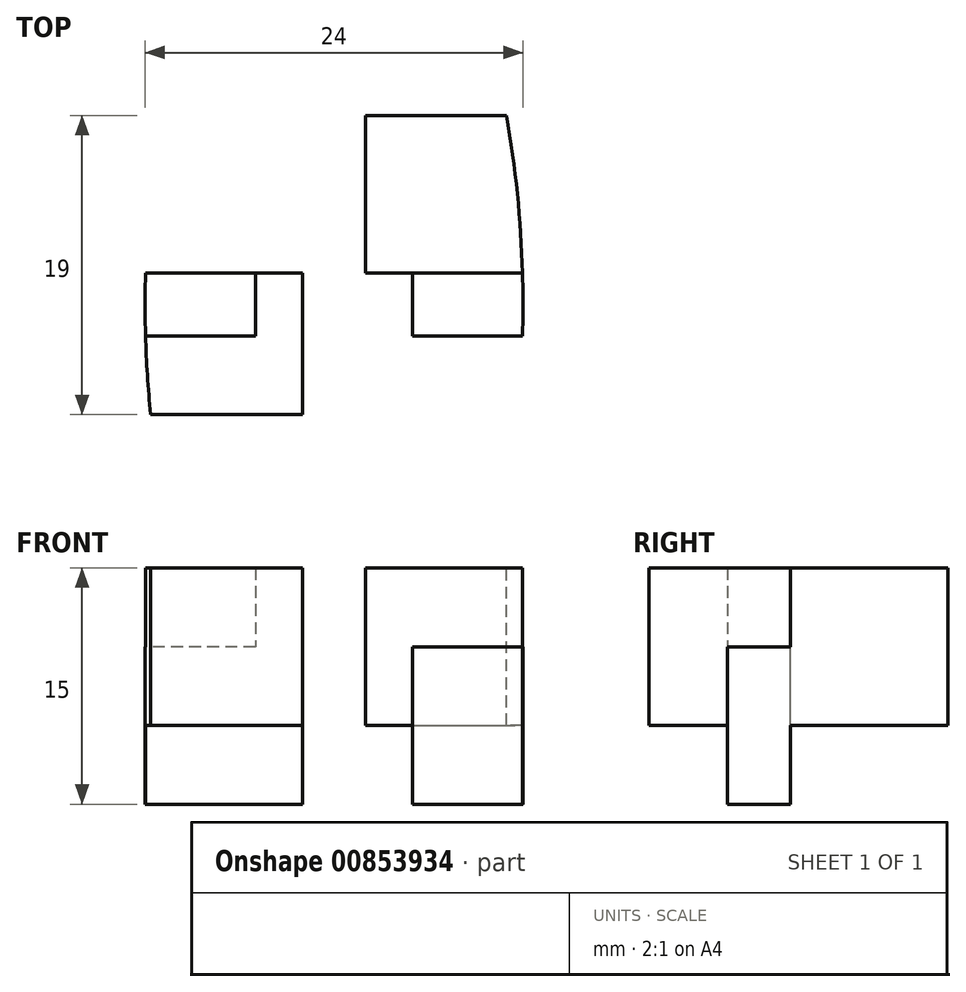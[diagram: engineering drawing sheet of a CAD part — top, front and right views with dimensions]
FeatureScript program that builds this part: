
annotation { "Feature Type Name" : "Feature", "Feature Type Description" : "" }
export const myFeature = defineFeature(function(context is Context, id is Id, definition is map)
    precondition{}
    {
        {
            var Q0;
            Q0=qCreatedBy(makeId("Top.planeOp"),FACE);
            var sketch = newSketch(context, id + "F0", { "sketchPlane" : qUnion([Q0])});
            skCircle(sketch, "E0", {"center": v(0, 57) * mm, "radius": 2 * mm});
            skLineSegment(sketch, "E1", {"start": v(12, 0) * mm, "end": v(57, 0) * mm});
            skLineSegment(sketch, "E2", {"start": v(0, 12) * mm, "end": v(-10.95, 12) * mm});
            skLineSegment(sketch, "E3", {"start": v(-10.95, 12) * mm, "end": v(10.95, 12) * mm});
            skLineSegment(sketch, "E4", {"start": v(0, -7) * mm, "end": v(-11.64, -7) * mm});
            skLineSegment(sketch, "E5", {"start": v(-11.64, -7) * mm, "end": v(-2, -7) * mm});
            skLineSegment(sketch, "E6", {"start": v(0, -2) * mm, "end": v(11.97, -2) * mm});
            skLineSegment(sketch, "E7", {"start": v(11.97, -2) * mm, "end": v(-11.97, -2) * mm});
            skLineSegment(sketch, "E8", {"start": v(0, 2) * mm, "end": v(-11.97, 2) * mm});
            skLineSegment(sketch, "E9", {"start": v(-11.97, 2) * mm, "end": v(11.97, 2) * mm});
            skLineSegment(sketch, "E10", {"start": v(0, 2) * mm, "end": v(-2, 2) * mm});
            skLineSegment(sketch, "E11", {"start": v(-2, 2) * mm, "end": v(-2, 57) * mm});
            skLineSegment(sketch, "E12", {"start": v(-2, 57) * mm, "end": v(2, 57) * mm});
            skLineSegment(sketch, "E13", {"start": v(2, 57) * mm, "end": v(2, 2) * mm});
            skCircle(sketch, "E14", {"center": v(0, -57) * mm, "radius": 2 * mm});
            skLineSegment(sketch, "E15", {"start": v(2, 2) * mm, "end": v(2, -57) * mm});
            skLineSegment(sketch, "E16", {"start": v(-2, 2) * mm, "end": v(-2, -57) * mm});
            skLineSegment(sketch, "E17", {"start": v(-5, 0) * mm, "end": v(-5, 57) * mm});
            skLineSegment(sketch, "E18", {"start": v(5, 0) * mm, "end": v(5, -57) * mm});
            skLineSegment(sketch, "E19", {"start": v(-5, 0) * mm, "end": v(-5, -57) * mm});
            skArc(sketch, "E20", {"start": v(5, -57) * mm, "mid": v(0, -62) * mm, "end": v(-5, -57) * mm});
            skLineSegment(sketch, "E21", {"start": v(5, 0) * mm, "end": v(5, 57) * mm});
            skArc(sketch, "E22", {"start": v(-5, 57) * mm, "mid": v(0, 62) * mm, "end": v(5, 57) * mm});
            skLineSegment(sketch, "E23.trimOffspring", {"start": v(0, -7) * mm, "end": v(11.64, -7) * mm});
            skLineSegment(sketch, "E24.trimOffspring", {"start": v(0, -55) * mm, "end": v(0, -57) * mm});
            skArc(sketch, "E25.trimOffspring", {"start": v(11.64, -7) * mm, "mid": v(11.95, 2.52) * mm, "end": v(10.95, 12) * mm});
            skArc(sketch, "E26.trimOffspring", {"start": v(-10.95, 12) * mm, "mid": v(-11.95, 2.52) * mm, "end": v(-11.64, -7) * mm});
            skLineSegment(sketch, "E27.trimOffspring", {"start": v(0, 55) * mm, "end": v(0, 57) * mm});
            skLineSegment(sketch, "E28.trimOffspring", {"start": v(-12, 0) * mm, "end": v(-57, 0) * mm});
            skSolve(sketch);
        }
        {
            var Q0;
            {var subQ0=sQuery(id+"F0.wireOp",EDGE,"E26.trimOffspring");var subQ1=sQuery(id+"F0.wireOp",EDGE,"E3");var subQ2=makeQuery(id+"F0.imprint","INTERSECT",VERTEX,{"derivedFrom":[subQ1,subQ0]});Q0=makeQuery(id+"F0.imprint","IMPRINT",FACE,{"disambiguationData":[TD([[makeQuery(id+"F0.imprint","IMPRINT",EDGE,{"disambiguationData":[TD([[subQ2,-1.0]])],"derivedFrom":subQ1}),-1.0]])]});}
            var Q1;
            {var subQ0=sQuery(id+"F0.wireOp",EDGE,"E26.trimOffspring");var subQ1=sQuery(id+"F0.wireOp",EDGE,"E5");var subQ2=makeQuery(id+"F0.imprint","INTERSECT",VERTEX,{"derivedFrom":[subQ1,subQ0]});Q1=makeQuery(id+"F0.imprint","IMPRINT",FACE,{"disambiguationData":[TD([[makeQuery(id+"F0.imprint","IMPRINT",EDGE,{"disambiguationData":[TD([[subQ2,-1.0]])],"derivedFrom":subQ1}),1.0]])]});}
            var Q2;
            {var subQ0=sQuery(id+"F0.wireOp",EDGE,"E16");var subQ5=sQuery(id+"F0.wireOp",EDGE,"E7");var subQ6=makeQuery(id+"F0.imprint","INTERSECT",VERTEX,{"derivedFrom":[subQ5,subQ0]});Q2=makeQuery(id+"F0.imprint","IMPRINT",FACE,{"disambiguationData":[TD([[makeQuery(id+"F0.imprint","IMPRINT",EDGE,{"disambiguationData":[TD([[subQ6,-1.0]])],"derivedFrom":subQ5}),1.0]])]});}
            var Q3;
            {var subQ0=sQuery(id+"F0.wireOp",EDGE,"E18");var subQ1=sQuery(id+"F0.wireOp",EDGE,"E7");var subQ2=makeQuery(id+"F0.imprint","INTERSECT",VERTEX,{"derivedFrom":[subQ1,subQ0]});Q3=makeQuery(id+"F0.imprint","IMPRINT",FACE,{"disambiguationData":[TD([[makeQuery(id+"F0.imprint","IMPRINT",EDGE,{"disambiguationData":[TD([[subQ2,-1.0]])],"derivedFrom":subQ1}),1.0]])]});}
            var Q4;
            {var subQ0=sQuery(id+"F0.wireOp",EDGE,"E25.trimOffspring");var subQ1=sQuery(id+"F0.wireOp",EDGE,"E7");var subQ2=makeQuery(id+"F0.imprint","INTERSECT",VERTEX,{"derivedFrom":[subQ1,subQ0]});Q4=makeQuery(id+"F0.imprint","IMPRINT",FACE,{"disambiguationData":[TD([[makeQuery(id+"F0.imprint","IMPRINT",EDGE,{"disambiguationData":[TD([[subQ2,-1.0]])],"derivedFrom":subQ1}),1.0]])]});}
            var Q5;
            {var subQ7=sQuery(id+"F0.wireOp",EDGE,"E25.trimOffspring");var subQ10=makeQuery(id+"F0.imprint","IMPRINT",VERTEX,{"derivedFrom":subQ7});Q5=makeQuery(id+"F0.imprint","IMPRINT",FACE,{"disambiguationData":[TD([[makeQuery(id+"F0.imprint","IMPRINT",EDGE,{"disambiguationData":[TD([[subQ10,1.0]])],"derivedFrom":subQ7}),1.0]])]});}
            var Q6;
            {var subQ5=sQuery(id+"F0.wireOp",EDGE,"E16");var subQ7=sQuery(id+"F0.wireOp",EDGE,"E7");var subQ8=makeQuery(id+"F0.imprint","INTERSECT",VERTEX,{"derivedFrom":[subQ7,subQ5]});Q6=makeQuery(id+"F0.imprint","IMPRINT",FACE,{"disambiguationData":[TD([[makeQuery(id+"F0.imprint","IMPRINT",EDGE,{"disambiguationData":[TD([[subQ8,-1.0]])],"derivedFrom":subQ7}),-1.0]])]});}
            var Q7;
            {var subQ0=sQuery(id+"F0.wireOp",EDGE,"E17");var subQ1=sQuery(id+"F0.wireOp",EDGE,"E3");var subQ2=makeQuery(id+"F0.imprint","INTERSECT",VERTEX,{"derivedFrom":[subQ1,subQ0]});Q7=makeQuery(id+"F0.imprint","IMPRINT",FACE,{"disambiguationData":[TD([[makeQuery(id+"F0.imprint","IMPRINT",EDGE,{"disambiguationData":[TD([[subQ2,-1.0]])],"derivedFrom":subQ1}),-1.0]])]});}
            var Q8;
            {var subQ0=sQuery(id+"F0.wireOp",EDGE,"E21");var subQ1=sQuery(id+"F0.wireOp",EDGE,"E3");var subQ2=makeQuery(id+"F0.imprint","INTERSECT",VERTEX,{"derivedFrom":[subQ1,subQ0]});Q8=makeQuery(id+"F0.imprint","IMPRINT",FACE,{"disambiguationData":[TD([[makeQuery(id+"F0.imprint","IMPRINT",EDGE,{"disambiguationData":[TD([[subQ2,1.0]])],"derivedFrom":subQ1}),-1.0]])]});}
            var Q9;
            {var subQ0=sQuery(id+"F0.wireOp",EDGE,"E25.trimOffspring");var subQ1=sQuery(id+"F0.wireOp",EDGE,"E3");var subQ2=makeQuery(id+"F0.imprint","INTERSECT",VERTEX,{"derivedFrom":[subQ1,subQ0]});Q9=makeQuery(id+"F0.imprint","IMPRINT",FACE,{"disambiguationData":[TD([[makeQuery(id+"F0.imprint","IMPRINT",EDGE,{"disambiguationData":[TD([[subQ2,1.0]])],"derivedFrom":subQ1}),-1.0]])]});}
            var Q10;
            {var subQ1=sQuery(id+"F0.wireOp",EDGE,"E18");var subQ3=sQuery(id+"F0.wireOp",EDGE,"E7");var subQ4=makeQuery(id+"F0.imprint","INTERSECT",VERTEX,{"derivedFrom":[subQ3,subQ1]});Q10=makeQuery(id+"F0.imprint","IMPRINT",FACE,{"disambiguationData":[TD([[makeQuery(id+"F0.imprint","IMPRINT",EDGE,{"disambiguationData":[TD([[subQ4,-1.0]])],"derivedFrom":subQ3}),-1.0]])]});}
            var Q11;
            {var subQ7=sQuery(id+"F0.wireOp",EDGE,"E26.trimOffspring");var subQ10=makeQuery(id+"F0.imprint","IMPRINT",VERTEX,{"derivedFrom":subQ7});Q11=makeQuery(id+"F0.imprint","IMPRINT",FACE,{"disambiguationData":[TD([[makeQuery(id+"F0.imprint","IMPRINT",EDGE,{"disambiguationData":[TD([[subQ10,1.0]])],"derivedFrom":subQ7}),1.0]])]});}
            extrude(context, id + "F1", {"entities" : qUnion([Q0, Q1, Q2, Q3, Q4, Q5, Q6, Q7, Q8, Q9, Q10, Q11]), "oppositeDirection" : true, "depth" : 5 * mm, "offsetDistance" : 25 * mm});
        }
        {
            var Q0;
            {var subQ7=sQuery(id+"F0.wireOp",EDGE,"E26.trimOffspring");var subQ10=makeQuery(id+"F0.imprint","IMPRINT",VERTEX,{"derivedFrom":subQ7});Q0=makeQuery(id+"F0.imprint","IMPRINT",FACE,{"disambiguationData":[TD([[makeQuery(id+"F0.imprint","IMPRINT",EDGE,{"disambiguationData":[TD([[subQ10,1.0]])],"derivedFrom":subQ7}),1.0]])]});}
            var Q1;
            {var subQ5=sQuery(id+"F0.wireOp",EDGE,"E16");var subQ7=sQuery(id+"F0.wireOp",EDGE,"E7");var subQ8=makeQuery(id+"F0.imprint","INTERSECT",VERTEX,{"derivedFrom":[subQ7,subQ5]});Q1=makeQuery(id+"F0.imprint","IMPRINT",FACE,{"disambiguationData":[TD([[makeQuery(id+"F0.imprint","IMPRINT",EDGE,{"disambiguationData":[TD([[subQ8,-1.0]])],"derivedFrom":subQ7}),-1.0]])]});}
            var Q2;
            {var subQ0=sQuery(id+"F0.wireOp",EDGE,"E10");Q2=makeQuery(id+"F0.imprint","IMPRINT",FACE,{"disambiguationData":[TD([[makeQuery(id+"F0.imprint","IMPRINT",EDGE,{"derivedFrom":subQ0}),1.0]])]});}
            var Q3;
            {var subQ1=sQuery(id+"F0.wireOp",EDGE,"E18");var subQ3=sQuery(id+"F0.wireOp",EDGE,"E7");var subQ4=makeQuery(id+"F0.imprint","INTERSECT",VERTEX,{"derivedFrom":[subQ3,subQ1]});Q3=makeQuery(id+"F0.imprint","IMPRINT",FACE,{"disambiguationData":[TD([[makeQuery(id+"F0.imprint","IMPRINT",EDGE,{"disambiguationData":[TD([[subQ4,-1.0]])],"derivedFrom":subQ3}),-1.0]])]});}
            var Q4;
            {var subQ7=sQuery(id+"F0.wireOp",EDGE,"E25.trimOffspring");var subQ10=makeQuery(id+"F0.imprint","IMPRINT",VERTEX,{"derivedFrom":subQ7});Q4=makeQuery(id+"F0.imprint","IMPRINT",FACE,{"disambiguationData":[TD([[makeQuery(id+"F0.imprint","IMPRINT",EDGE,{"disambiguationData":[TD([[subQ10,1.0]])],"derivedFrom":subQ7}),1.0]])]});}
            extrude(context, id + "F2", {"entities" : qUnion([Q0, Q1, Q2, Q3, Q4]), "operationType" : NewBodyOperationType.ADD, "oppositeDirection" : true, "depth" : 10 * mm, "offsetDistance" : 25 * mm, "hasSecondDirection" : true, "secondDirectionOppositeDirection" : true, "secondDirectionDepth" : 5 * mm});
        }
        {
            var Q0;
            {var subQ5=sQuery(id+"F0.wireOp",EDGE,"E22");Q0=makeQuery(id+"F0.imprint","IMPRINT",FACE,{"disambiguationData":[TD([[makeQuery(id+"F0.imprint","IMPRINT",EDGE,{"derivedFrom":subQ5}),-1.0]])]});}
            var Q1;
            {var subQ0=sQuery(id+"F0.wireOp",EDGE,"E17");var subQ1=sQuery(id+"F0.wireOp",EDGE,"E3");var subQ2=makeQuery(id+"F0.imprint","INTERSECT",VERTEX,{"derivedFrom":[subQ1,subQ0]});Q1=makeQuery(id+"F0.imprint","IMPRINT",FACE,{"disambiguationData":[TD([[makeQuery(id+"F0.imprint","IMPRINT",EDGE,{"disambiguationData":[TD([[subQ2,-1.0]])],"derivedFrom":subQ1}),-1.0]])]});}
            var Q2;
            {var subQ0=sQuery(id+"F0.wireOp",EDGE,"E21");var subQ1=sQuery(id+"F0.wireOp",EDGE,"E3");var subQ2=makeQuery(id+"F0.imprint","INTERSECT",VERTEX,{"derivedFrom":[subQ1,subQ0]});Q2=makeQuery(id+"F0.imprint","IMPRINT",FACE,{"disambiguationData":[TD([[makeQuery(id+"F0.imprint","IMPRINT",EDGE,{"disambiguationData":[TD([[subQ2,1.0]])],"derivedFrom":subQ1}),-1.0]])]});}
            var Q3;
            {var subQ5=sQuery(id+"F0.wireOp",EDGE,"E16");var subQ7=sQuery(id+"F0.wireOp",EDGE,"E7");var subQ8=makeQuery(id+"F0.imprint","INTERSECT",VERTEX,{"derivedFrom":[subQ7,subQ5]});Q3=makeQuery(id+"F0.imprint","IMPRINT",FACE,{"disambiguationData":[TD([[makeQuery(id+"F0.imprint","IMPRINT",EDGE,{"disambiguationData":[TD([[subQ8,-1.0]])],"derivedFrom":subQ7}),-1.0]])]});}
            var Q4;
            {var subQ0=sQuery(id+"F0.wireOp",EDGE,"E18");var subQ1=sQuery(id+"F0.wireOp",EDGE,"E7");var subQ2=makeQuery(id+"F0.imprint","INTERSECT",VERTEX,{"derivedFrom":[subQ1,subQ0]});Q4=makeQuery(id+"F0.imprint","IMPRINT",FACE,{"disambiguationData":[TD([[makeQuery(id+"F0.imprint","IMPRINT",EDGE,{"disambiguationData":[TD([[subQ2,-1.0]])],"derivedFrom":subQ1}),1.0]])]});}
            var Q5;
            {var subQ0=sQuery(id+"F0.wireOp",EDGE,"E16");var subQ5=sQuery(id+"F0.wireOp",EDGE,"E7");var subQ6=makeQuery(id+"F0.imprint","INTERSECT",VERTEX,{"derivedFrom":[subQ5,subQ0]});Q5=makeQuery(id+"F0.imprint","IMPRINT",FACE,{"disambiguationData":[TD([[makeQuery(id+"F0.imprint","IMPRINT",EDGE,{"disambiguationData":[TD([[subQ6,-1.0]])],"derivedFrom":subQ5}),1.0]])]});}
            var Q6;
            {var subQ13=sQuery(id+"F0.wireOp",EDGE,"E20");Q6=makeQuery(id+"F0.imprint","IMPRINT",FACE,{"disambiguationData":[TD([[makeQuery(id+"F0.imprint","IMPRINT",EDGE,{"derivedFrom":subQ13}),-1.0]])]});}
            var Q7;
            {var subQ1=sQuery(id+"F0.wireOp",EDGE,"E18");var subQ3=sQuery(id+"F0.wireOp",EDGE,"E7");var subQ4=makeQuery(id+"F0.imprint","INTERSECT",VERTEX,{"derivedFrom":[subQ3,subQ1]});Q7=makeQuery(id+"F0.imprint","IMPRINT",FACE,{"disambiguationData":[TD([[makeQuery(id+"F0.imprint","IMPRINT",EDGE,{"disambiguationData":[TD([[subQ4,-1.0]])],"derivedFrom":subQ3}),-1.0]])]});}
            extrude(context, id + "F3", {"entities" : qUnion([Q0, Q1, Q2, Q3, Q4, Q5, Q6, Q7]), "operationType" : NewBodyOperationType.ADD, "depth" : 5 * mm, "offsetDistance" : 25 * mm});
        }
    });
